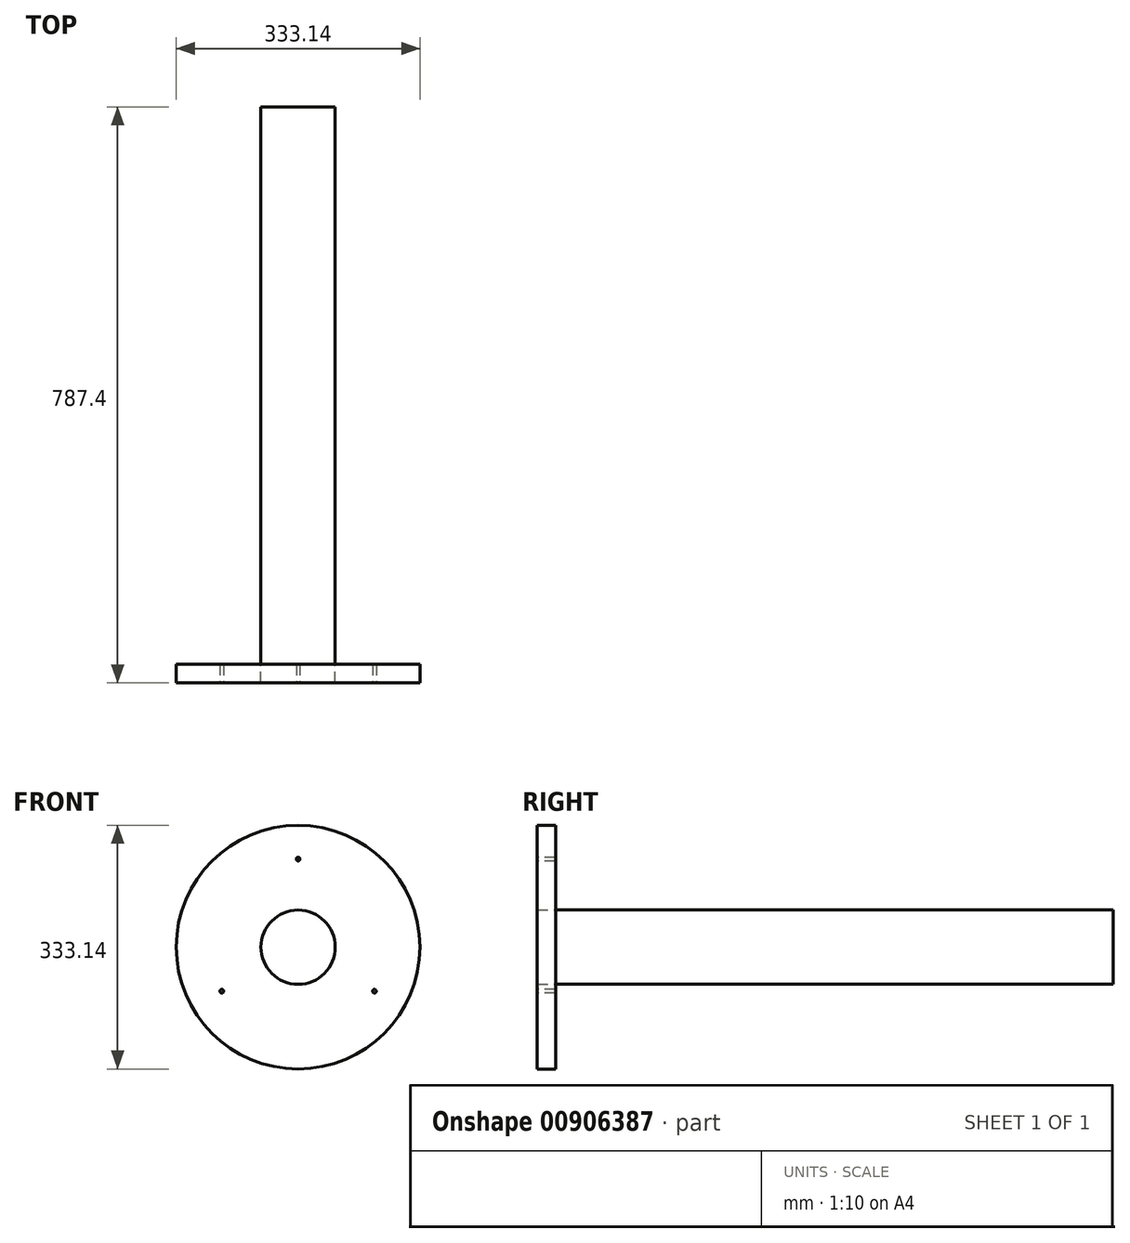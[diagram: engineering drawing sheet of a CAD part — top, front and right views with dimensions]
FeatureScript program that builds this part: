
annotation { "Feature Type Name" : "Feature", "Feature Type Description" : "" }
export const myFeature = defineFeature(function(context is Context, id is Id, definition is map)
    precondition{}
    {
        {
            var Q0;
            Q0=qCreatedBy(makeId("Front.planeOp"),FACE);
            var sketch = newSketch(context, id + "F0", { "sketchPlane" : qUnion([Q0])});
            skCircle(sketch, "E0", {"center": v(0, 0) * mm, "radius": 50.8 * mm});
            skSolve(sketch);
        }
        {
            var Q0;
            Q0 = qSketchRegion(id + "F0", true);
            extrude(context, id + "F1", {"entities" : qUnion([Q0]), "depth" : 762 * mm, "offsetDistance" : 25.4 * mm});
        }
        {
            var Q0;
            Q0=makeQuery(id+"F1.opExtrude","CAP_FACE",FACE,{"disambiguationData":[OSD([sQuery(id+"F0.wireOp",EDGE,"E0")])],"isStart":false});
            var sketch = newSketch(context, id + "F2", { "sketchPlane" : qUnion([Q0])});
            skCircle(sketch, "E1", {"center": v(0, 0) * mm, "radius": 166.57 * mm});
            skSolve(sketch);
        }
        {
            var Q0;
            Q0=makeQuery(id+"F2.imprint","IMPRINT",FACE,{"disambiguationData":[TD([[makeQuery(id+"F2.imprint","IMPRINT",EDGE,{"derivedFrom":sQuery(id+"F2.wireOp",EDGE,"E1")}),1.0]])]});
            extrude(context, id + "F3", {"entities" : qUnion([Q0]), "depth" : 25.4 * mm, "offsetDistance" : 25.4 * mm});
        }
        {
            var Q0;
            Q0=makeQuery(id+"F3.opExtrude","CAP_FACE",FACE,{"disambiguationData":[OSD([sQuery(id+"F0.wireOp",EDGE,"E0"),sQuery(id+"F2.wireOp",EDGE,"E1")])],"isStart":false});
            var sketch = newSketch(context, id + "F4", { "sketchPlane" : qUnion([Q0])});
            skCircle(sketch, "E2", {"center": v(0, 120.4) * mm, "radius": 18.66 * mm});
            skCircle(sketch, "E3.1.0", {"center": v(-104.28, -60.2) * mm, "radius": 18.66 * mm});
            skCircle(sketch, "E3.2.0", {"center": v(104.28, -60.2) * mm, "radius": 18.66 * mm});
            skPoint(sketch, "E3.center", {"position": v(0, 0) * mm});
            skSolve(sketch);
        }
        {
            var Q0;
            Q0=sQuery(id+"F4.wireOp",VERTEX,"E2.center");
            var Q1;
            Q1=sQuery(id+"F4.wireOp",VERTEX,"E3.2.0.center");
            var Q2;
            Q2=sQuery(id+"F4.wireOp",VERTEX,"E3.1.0.center");
            var Q3;
            Q3=makeQuery(id+"F3.opExtrude","SWEPT_BODY",BODY,{"disambiguationData":[OSD([sQuery(id+"F0.wireOp",EDGE,"E0"),sQuery(id+"F2.wireOp",EDGE,"E1")])]});
            hole(context, id + "F5", {"style" : HoleStyle.SIMPLE, "endStyle" : HoleEndStyle.THROUGH, "standardTappedOrClearance" : lookupTablePath({ "standard" : "ISO", "engagement" : "75%", "pitch" : "1 mm", "size" : "M6", "type" : "Tapped" }), "standardBlindInLast" : lookupTablePath({ "standard" : "ISO", "engagement" : "75%", "pitch" : "1 mm", "size" : "M6", "type" : "Tapped" }), "holeDiameter" : 5 * mm, "majorDiameter" : 6 * mm, "showTappedDepth" : true, "isTappedThrough" : true, "tappedDepth" : 12.7 * mm, "tapClearance" : 3, "locations" : qUnion([Q0, Q1, Q2]), "scope" : qUnion([Q3])});
        }
    });
